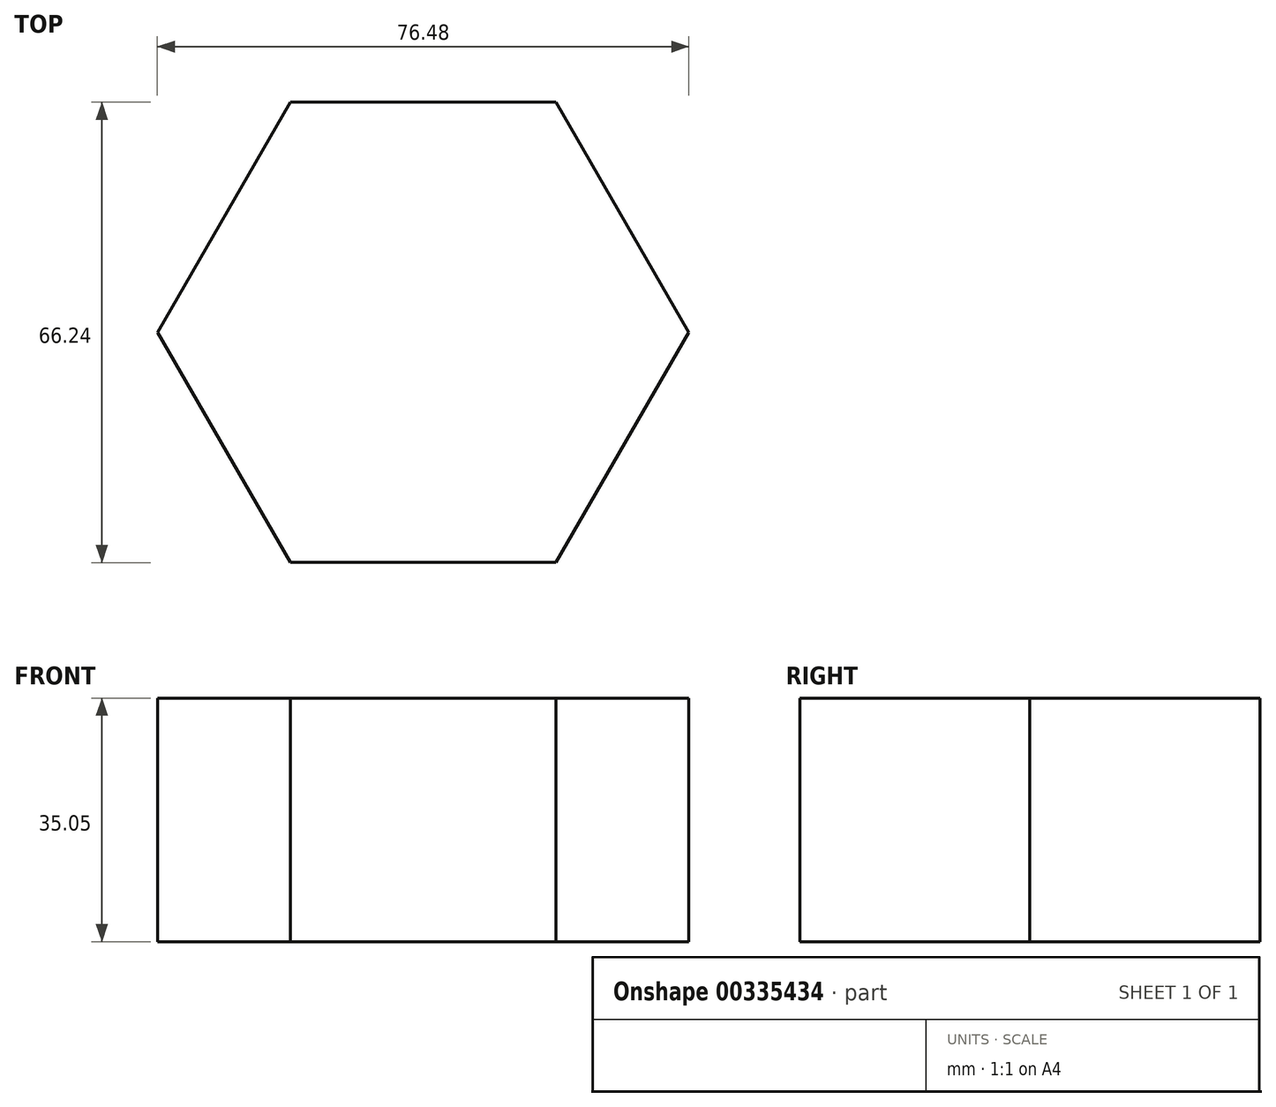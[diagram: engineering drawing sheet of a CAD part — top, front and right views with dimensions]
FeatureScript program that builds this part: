
annotation { "Feature Type Name" : "Feature", "Feature Type Description" : "" }
export const myFeature = defineFeature(function(context is Context, id is Id, definition is map)
    precondition{}
    {
        {
            var Q0;
            Q0=qCreatedBy(makeId("Top.planeOp"),FACE);
            var sketch = newSketch(context, id + "F0", { "sketchPlane" : qUnion([Q0])});
            skCircle(sketch, "E0.cCircle", {"center": v(0, 0) * mm, "radius": 33.12 * mm, "construction": true});
            skLineSegment(sketch, "E0.0", {"start": v(-19.12, 33.12) * mm, "end": v(19.12, 33.12) * mm});
            skLineSegment(sketch, "E0.1", {"start": v(19.12, 33.12) * mm, "end": v(38.24, 0) * mm});
            skLineSegment(sketch, "E0.2", {"start": v(38.24, 0) * mm, "end": v(19.12, -33.12) * mm});
            skLineSegment(sketch, "E0.3", {"start": v(19.12, -33.12) * mm, "end": v(-19.12, -33.12) * mm});
            skLineSegment(sketch, "E0.4", {"start": v(-19.12, -33.12) * mm, "end": v(-38.24, 0) * mm});
            skLineSegment(sketch, "E0.5", {"start": v(-38.24, 0) * mm, "end": v(-19.12, 33.12) * mm});
            skPoint(sketch, "E0.0.midPoint", {"position": v(0, 33.12) * mm});
            skSolve(sketch);
        }
        {
            var Q0;
            Q0=makeQuery(id+"F0.imprint","IMPRINT",FACE,{"disambiguationData":[TD([[makeQuery(id+"F0.imprint","IMPRINT",EDGE,{"derivedFrom":sQuery(id+"F0.wireOp",EDGE,"E0.0")}),-1.0]])]});
            extrude(context, id + "F1", {"entities" : qUnion([Q0]), "depth" : 35.05 * mm});
        }
    });
